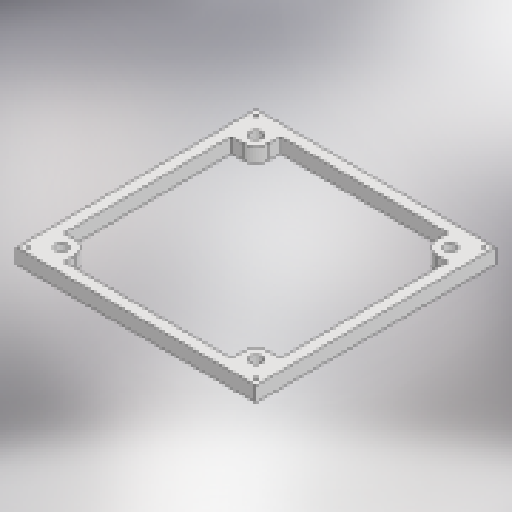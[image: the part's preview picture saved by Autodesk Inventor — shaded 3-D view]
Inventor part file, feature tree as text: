
AUTODESK INVENTOR PART (.ipt)
format: ipt  version: 2024 (Build 280153000, 153)  size: 227,328 bytes
history: native  units: in
note: dims shown in document units (in); Inventor stores cm internally (conversion verified against a paired STEP export)
features: extrude x2, projected_geometry x2
ambient origin geometry x8: Origin, YZ Plane, XZ Plane, XY Plane, X Axis, Y Axis, Z Axis, Center Point
bodies: Solid1 (feature_tree)
feature tree (4):
  extrude  "Extrusion1"  Depth=4.0in
  extrude  "Extrusion2"  Depth=4.0in
  projected_geometry  "Projected Loop1"
  projected_geometry  "Projected Loop2"
